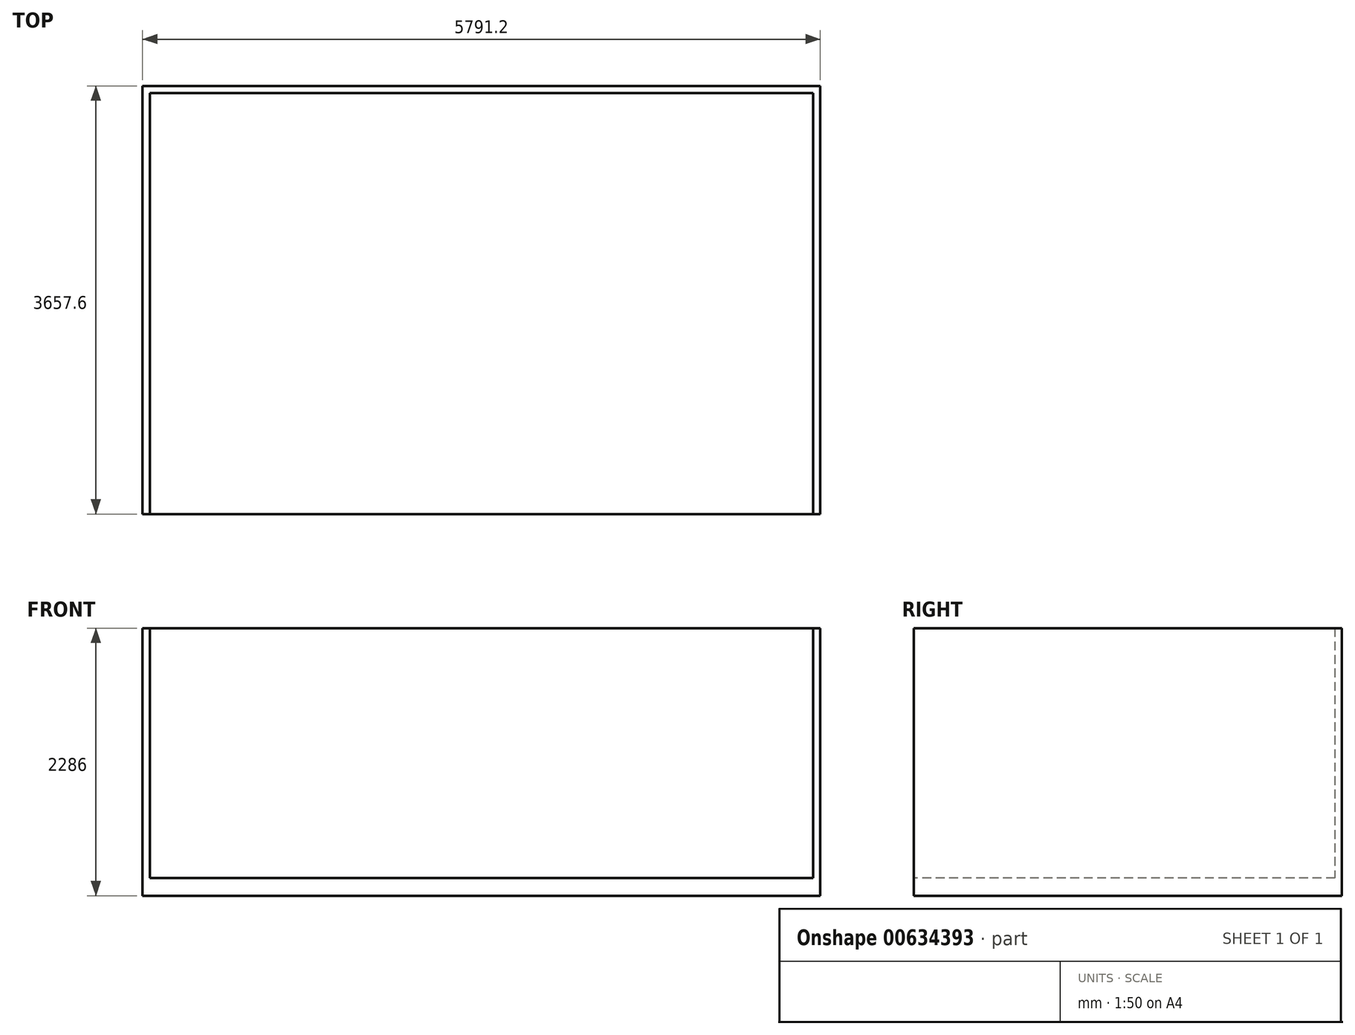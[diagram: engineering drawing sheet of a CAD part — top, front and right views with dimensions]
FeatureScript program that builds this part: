
annotation { "Feature Type Name" : "Feature", "Feature Type Description" : "" }
export const myFeature = defineFeature(function(context is Context, id is Id, definition is map)
    precondition{}
    {
        {
            var Q0;
            Q0=qCreatedBy(makeId("Top.planeOp"),FACE);
            var sketch = newSketch(context, id + "F0", { "sketchPlane" : qUnion([Q0])});
            skLineSegment(sketch, "E0.bottom", {"start": v(-2893.2, 2151.38) * mm, "end": v(2898, 2151.38) * mm});
            skLineSegment(sketch, "E0.top", {"start": v(-2893.2, -1506.22) * mm, "end": v(2898, -1506.22) * mm});
            skLineSegment(sketch, "E0.left", {"start": v(-2893.2, 2151.38) * mm, "end": v(-2893.2, -1506.22) * mm});
            skLineSegment(sketch, "E0.right", {"start": v(2898, 2151.38) * mm, "end": v(2898, -1506.22) * mm});
            skSolve(sketch);
        }
        {
            var Q0;
            Q0=makeQuery(id+"F0.imprint","IMPRINT",FACE,{"disambiguationData":[TD([[makeQuery(id+"F0.imprint","IMPRINT",EDGE,{"derivedFrom":sQuery(id+"F0.wireOp",EDGE,"E0.bottom")}),-1.0]])]});
            extrude(context, id + "F1", {"entities" : qUnion([Q0]), "depth" : 152.4 * mm, "offsetDistance" : 30.48 * mm});
        }
        {
            var Q0;
            Q0=makeQuery(id+"F1.opExtrude","CAP_FACE",FACE,{"disambiguationData":[OSD([sQuery(id+"F0.wireOp",EDGE,"E0.bottom"),sQuery(id+"F0.wireOp",EDGE,"E0.top"),sQuery(id+"F0.wireOp",EDGE,"E0.left"),sQuery(id+"F0.wireOp",EDGE,"E0.right")])],"isStart":false});
            var sketch = newSketch(context, id + "F2", { "sketchPlane" : qUnion([Q0])});
            skLineSegment(sketch, "E1.bottom", {"start": v(-2893.2, 2151.38) * mm, "end": v(2898, 2151.38) * mm});
            skLineSegment(sketch, "E1.top", {"start": v(-2893.2, 2090.42) * mm, "end": v(2898, 2090.42) * mm});
            skLineSegment(sketch, "E1.left", {"start": v(-2893.2, 2151.38) * mm, "end": v(-2893.2, 2090.42) * mm});
            skLineSegment(sketch, "E1.right", {"start": v(2898, 2151.38) * mm, "end": v(2898, 2090.42) * mm});
            skSolve(sketch);
        }
        {
            var Q0;
            Q0=makeQuery(id+"F2.imprint","IMPRINT",FACE,{"disambiguationData":[TD([[makeQuery(id+"F2.imprint","IMPRINT",EDGE,{"derivedFrom":sQuery(id+"F2.wireOp",EDGE,"E1.bottom")}),-1.0]])]});
            extrude(context, id + "F3", {"entities" : qUnion([Q0]), "operationType" : NewBodyOperationType.ADD, "depth" : 2133.6 * mm, "offsetDistance" : 30.48 * mm});
        }
        {
            var Q0;
            Q0=makeQuery(id+"F1.opExtrude","CAP_FACE",FACE,{"disambiguationData":[OSD([sQuery(id+"F0.wireOp",EDGE,"E0.bottom"),sQuery(id+"F0.wireOp",EDGE,"E0.top"),sQuery(id+"F0.wireOp",EDGE,"E0.left"),sQuery(id+"F0.wireOp",EDGE,"E0.right")])],"isStart":false});
            var sketch = newSketch(context, id + "F4", { "sketchPlane" : qUnion([Q0])});
            skLineSegment(sketch, "E2.bottom", {"start": v(-2893.2, -1506.22) * mm, "end": v(-2832.23, -1506.22) * mm});
            skLineSegment(sketch, "E2.top", {"start": v(-2893.2, 2090.42) * mm, "end": v(-2832.23, 2090.42) * mm});
            skLineSegment(sketch, "E2.left", {"start": v(-2893.2, -1506.22) * mm, "end": v(-2893.2, 2090.42) * mm});
            skLineSegment(sketch, "E2.right", {"start": v(-2832.23, -1506.22) * mm, "end": v(-2832.23, 2090.42) * mm});
            skLineSegment(sketch, "E3.bottom", {"start": v(2898, 2090.42) * mm, "end": v(2837.05, 2090.42) * mm});
            skLineSegment(sketch, "E3.top", {"start": v(2898, -1506.22) * mm, "end": v(2837.05, -1506.22) * mm});
            skLineSegment(sketch, "E3.left", {"start": v(2898, 2090.42) * mm, "end": v(2898, -1506.22) * mm});
            skLineSegment(sketch, "E3.right", {"start": v(2837.05, 2090.42) * mm, "end": v(2837.05, -1506.22) * mm});
            skSolve(sketch);
        }
        {
            var Q0;
            Q0=makeQuery(id+"F4.imprint","IMPRINT",FACE,{"disambiguationData":[TD([[makeQuery(id+"F4.imprint","IMPRINT",EDGE,{"derivedFrom":sQuery(id+"F4.wireOp",EDGE,"E2.bottom")}),1.0]])]});
            var Q1;
            Q1=makeQuery(id+"F4.imprint","IMPRINT",FACE,{"disambiguationData":[TD([[makeQuery(id+"F4.imprint","IMPRINT",EDGE,{"derivedFrom":sQuery(id+"F4.wireOp",EDGE,"E3.bottom")}),-1.0]])]});
            extrude(context, id + "F5", {"entities" : qUnion([Q0, Q1]), "operationType" : NewBodyOperationType.ADD, "depth" : 2133.6 * mm, "offsetDistance" : 30.48 * mm});
        }
    });
